# Revit family: F1V_2903-2943-2607_OS275
name_source: partatom
category: Finestre
units: mm (PartAtom-declared; Revit-internal decimal feet)

## family parameters
Condiviso = No
Host = Muro
Numero OmniClass = 23.30.20.00
Punto di calcolo locali = No
Sempre verticale = Sì
Taglio con vuoti quando caricato = No
Titolo OmniClass = Windows

## types (4) — shared parameters
Chiusura muro = Per host
Costruzione analitica = <Nessuno>
Descrizione = Finestra vasistas
H_Max = 800 mm
H_Min = 400 mm  [stored 1.31234 ft]
L = 1300 mm  [stored 4.26509 ft]
L1 = 1300 mm  [stored 4.26509 ft]
L_Max = 1300 mm  [stored 4.26509 ft]
L_Min = 300 mm
L_fermavetro = 1236 mm  [stored 4.05512 ft]
L_vetro = 1224 mm  [stored 4.01575 ft]
Maniglia_alta = 1050 mm  [stored 3.44488 ft]
Maniglia_media = 500 mm  [stored 1.64042 ft]
Modello = OS2 75
Produttore = Secco Sistemi Spa
WARNING = Sì
n2_cerniere = 2
n2_scarichi = 2
n3_cerniere = 3
n3_scarichi = 3
n4_cerniere = 4
numero_cerniere = 3
numero_scarichi = 3

## per-type parameters (varying)
| type | Altezza | Altezza di default del davanzale | H | H1 | H_fermavetro | H_man | H_maniglia | H_vetro | Larghezza | MATERIALE | Maniglia_bassa | URL |
| Ottone | 700 mm  [stored 2.29659 ft] | 800 mm | 700 mm  [stored 2.29659 ft] | 700 mm  [stored 2.29659 ft] | 636 mm  [stored 2.08661 ft] | 350 mm | 350 mm | 624 mm  [stored 2.04724 ft] | 2000 mm  [stored 6.56168 ft] | Ottone | 350 mm |  |
| Acciaio zincato | 1000 mm  [stored 3.28084 ft] | 1000 mm  [stored 3.28084 ft] | 800 mm | 800 mm | 736 mm | 500 mm  [stored 1.64042 ft] | 500 mm  [stored 1.64042 ft] | 724 mm | 1500 mm  [stored 4.92126 ft] | Acciaio | 400 mm  [stored 1.31234 ft] |  |
| Acciaio inox | 1500 mm  [stored 4.92126 ft] | 800 mm | 800 mm | 800 mm | 736 mm | 500 mm  [stored 1.64042 ft] | 500 mm  [stored 1.64042 ft] | 724 mm | 1500 mm  [stored 4.92126 ft] | Acciaio inox, spazzolato | 400 mm  [stored 1.31234 ft] |  |
| Acciaio corten | 2000 mm  [stored 6.56168 ft] | 800 mm | 800 mm | 800 mm | 736 mm | 1050 mm  [stored 3.44488 ft] | 1050 mm  [stored 3.44488 ft] | 724 mm | 2000 mm  [stored 6.56168 ft] | Acciaio corten | 400 mm  [stored 1.31234 ft] | https://www.seccosistemi.com |

note: [stored X ft] marks values corroborated as IEEE doubles in the binary element streams (Revit-internal decimal feet)
